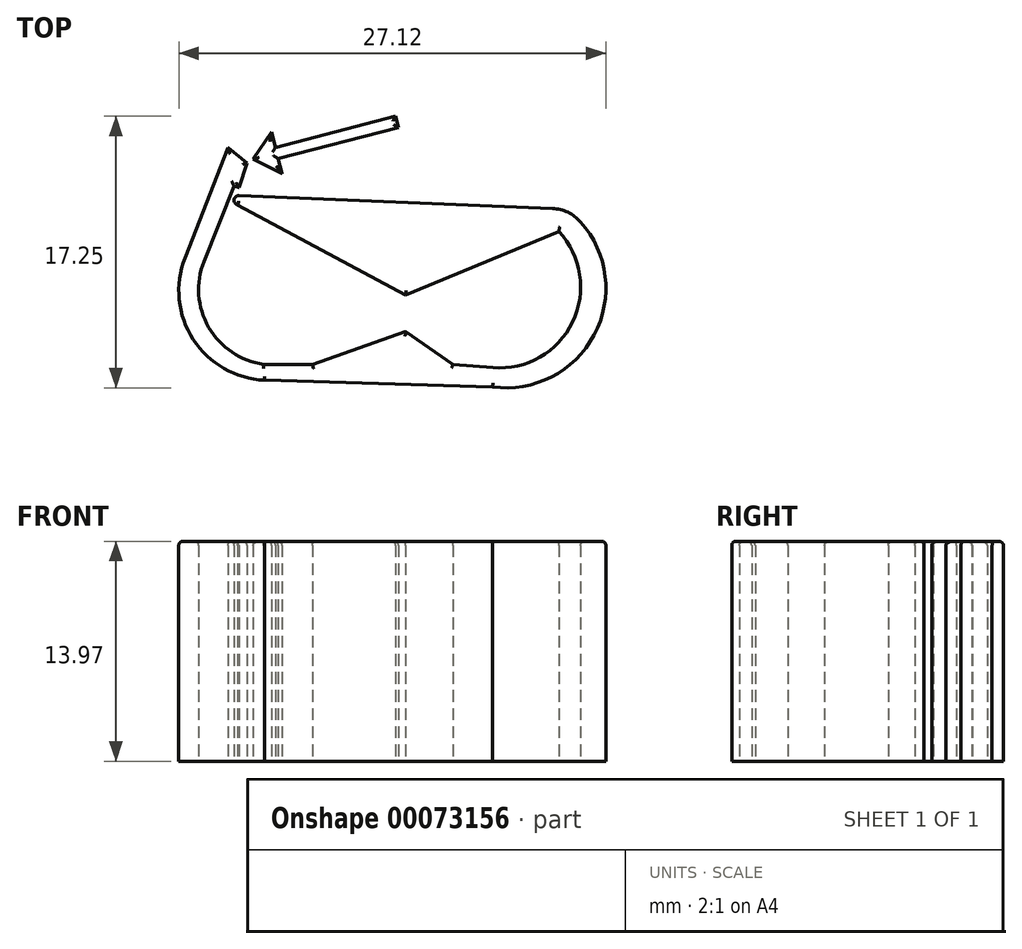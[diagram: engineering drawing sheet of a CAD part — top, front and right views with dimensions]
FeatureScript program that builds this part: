
annotation { "Feature Type Name" : "Feature", "Feature Type Description" : "" }
export const myFeature = defineFeature(function(context is Context, id is Id, definition is map)
    precondition{}
    {
        {
            var Q0;
            Q0=qCreatedBy(makeId("Top.planeOp"),FACE);
            var sketch = newSketch(context, id + "F0", { "sketchPlane" : qUnion([Q0])});
            skLineSegment(sketch, "E0", {"start": v(-9.02, 0) * mm, "end": v(-5.9, 0) * mm});
            skLineSegment(sketch, "E1", {"start": v(-5.9, 0) * mm, "end": v(0, 2.07) * mm});
            skLineSegment(sketch, "E2", {"start": v(0, 2.07) * mm, "end": v(3, 0) * mm});
            skLineSegment(sketch, "E3", {"start": v(-14.02, 6.76) * mm, "end": v(-11.27, 13.77) * mm});
            skLineSegment(sketch, "E4", {"start": v(-11.27, 13.77) * mm, "end": v(-10.08, 12.78) * mm});
            skLineSegment(sketch, "E5", {"start": v(-10.08, 12.78) * mm, "end": v(-10.6, 11.22) * mm});
            skLineSegment(sketch, "E6", {"start": v(-10.6, 11.22) * mm, "end": v(-10.9, 11.32) * mm});
            skLineSegment(sketch, "E7", {"start": v(-10.9, 11.32) * mm, "end": v(-12.81, 6.54) * mm});
            skArc(sketch, "E8", {"start": v(-12.81, 6.54) * mm, "mid": v(-12.5, 2.35) * mm, "end": v(-9.02, 0) * mm});
            skArc(sketch, "E9", {"start": v(-14.02, 6.76) * mm, "mid": v(-13.5, 1.58) * mm, "end": v(-8.97, -1) * mm});
            skLineSegment(sketch, "E10", {"start": v(-8.97, -1) * mm, "end": v(3.1, -1.36) * mm});
            skLineSegment(sketch, "E11", {"start": v(10.23, 9.86) * mm, "end": v(-10.6, 10.72) * mm});
            skLineSegment(sketch, "E12", {"start": v(0, 4.4) * mm, "end": v(9.72, 8.44) * mm});
            skLineSegment(sketch, "E13", {"start": v(3.1, -1.36) * mm, "end": v(5.52, -1.43) * mm});
            skLineSegment(sketch, "E14", {"start": v(3, 0) * mm, "end": v(5.54, -0.2) * mm});
            skArc(sketch, "E15", {"start": v(5.54, -0.2) * mm, "mid": v(10.6, 2.69) * mm, "end": v(9.72, 8.44) * mm});
            skArc(sketch, "E16", {"start": v(5.52, -1.43) * mm, "mid": v(12.22, 2.4) * mm, "end": v(10.23, 9.86) * mm});
            skLineSegment(sketch, "E17", {"start": v(-9.68, 13.04) * mm, "end": v(-7.85, 12.11) * mm});
            skLineSegment(sketch, "E18", {"start": v(-7.85, 12.11) * mm, "end": v(-8.1, 13.07) * mm});
            skLineSegment(sketch, "E19", {"start": v(-8.1, 13.07) * mm, "end": v(-0.46, 15.05) * mm});
            skLineSegment(sketch, "E20.MirrorCS", {"start": v(-8.28, 13.78) * mm, "end": v(-0.64, 15.76) * mm});
            skLineSegment(sketch, "E21.MirrorCS", {"start": v(-8.53, 14.74) * mm, "end": v(-8.28, 13.78) * mm});
            skLineSegment(sketch, "E22.MirrorCS", {"start": v(-9.68, 13.04) * mm, "end": v(-8.53, 14.74) * mm});
            skLineSegment(sketch, "E23", {"start": v(-0.64, 15.76) * mm, "end": v(-0.46, 15.05) * mm});
            skLineSegment(sketch, "E24", {"start": v(0, 4.4) * mm, "end": v(-10.68, 10.13) * mm});
            skArc(sketch, "E25", {"start": v(-10.6, 10.72) * mm, "mid": v(-10.9, 10.46) * mm, "end": v(-10.68, 10.13) * mm});
            skSolve(sketch);
        }
        {
            var Q0;
            Q0=makeQuery(id+"F0.imprint","IMPRINT",FACE,{"disambiguationData":[TD([[makeQuery(id+"F0.imprint","IMPRINT",EDGE,{"derivedFrom":sQuery(id+"F0.wireOp",EDGE,"9T2jLX1K-ABNv-7rBE-ews3-E361xKiuboZv")}),1.0]])]});
            var Q1;
            Q1=makeQuery(id+"F0.imprint","IMPRINT",FACE,{"disambiguationData":[TD([[makeQuery(id+"F0.imprint","IMPRINT",EDGE,{"derivedFrom":sQuery(id+"F0.wireOp",EDGE,"E0")}),-1.0]])]});
            var Q2;
            Q2=makeQuery(id+"F0.imprint","IMPRINT",FACE,{"disambiguationData":[TD([[makeQuery(id+"F0.imprint","IMPRINT",EDGE,{"derivedFrom":sQuery(id+"F0.wireOp",EDGE,"E17")}),1.0]])]});
            extrude(context, id + "F1", {"entities" : qUnion([Q0, Q1, Q2]), "depth" : 13.97 * mm});
        }
        {
            var Q0;
            Q0=makeQuery(id+"F1.opExtrude","SWEPT_EDGE",EDGE,{"disambiguationData":[OSD([sQuery(id+"F0.wireOp",EDGE,"E11"),sQuery(id+"F0.wireOp",EDGE,"E16")])]});
            fillet(context, id + "F2", {"entities" : qUnion([Q0]), "radius" : 2.54 * mm, "tangentPropagation" : true, "allowEdgeOverflow" : false});
        }
        {
            var Q0;
            Q0=makeQuery(id+"F1.opExtrude","CAP_FACE",FACE,{"disambiguationData":[OSD([sQuery(id+"F0.wireOp",EDGE,"E0"),sQuery(id+"F0.wireOp",EDGE,"E1"),sQuery(id+"F0.wireOp",EDGE,"E2"),sQuery(id+"F0.wireOp",EDGE,"E3"),sQuery(id+"F0.wireOp",EDGE,"E4"),sQuery(id+"F0.wireOp",EDGE,"E5"),sQuery(id+"F0.wireOp",EDGE,"E6"),sQuery(id+"F0.wireOp",EDGE,"E7"),sQuery(id+"F0.wireOp",EDGE,"E8"),sQuery(id+"F0.wireOp",EDGE,"E9"),sQuery(id+"F0.wireOp",EDGE,"E10"),sQuery(id+"F0.wireOp",EDGE,"E11"),sQuery(id+"F0.wireOp",EDGE,"E12"),sQuery(id+"F0.wireOp",EDGE,"E13"),sQuery(id+"F0.wireOp",EDGE,"E14"),sQuery(id+"F0.wireOp",EDGE,"E15"),sQuery(id+"F0.wireOp",EDGE,"E16"),sQuery(id+"F0.wireOp",EDGE,"E24"),sQuery(id+"F0.wireOp",EDGE,"E25")])],"isStart":false});
            var Q1;
            Q1=makeQuery(id+"F1.opExtrude","CAP_FACE",FACE,{"disambiguationData":[OSD([sQuery(id+"F0.wireOp",EDGE,"E17"),sQuery(id+"F0.wireOp",EDGE,"E18"),sQuery(id+"F0.wireOp",EDGE,"E19"),sQuery(id+"F0.wireOp",EDGE,"E20.MirrorCS"),sQuery(id+"F0.wireOp",EDGE,"E21.MirrorCS"),sQuery(id+"F0.wireOp",EDGE,"E22.MirrorCS"),sQuery(id+"F0.wireOp",EDGE,"E23")])],"isStart":false});
            fillet(context, id + "F3", {"entities" : qUnion([Q0, Q1]), "radius" : .25 * mm, "tangentPropagation" : true, "allowEdgeOverflow" : false});
        }
    });
